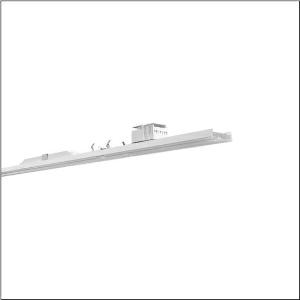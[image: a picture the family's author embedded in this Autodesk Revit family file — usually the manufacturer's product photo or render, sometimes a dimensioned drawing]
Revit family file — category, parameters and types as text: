
# Revit family: licross_r__21_recessed_mo_52tl14dnd7xf_36eb
name_source: partatom
category: Lighting Fixtures
units: mm (PartAtom-declared; Revit-internal decimal feet)

## family parameters
Cut with Voids When Loaded = No
Host = Face
Light Source = No
Part Type = Normal
Room Calculation Point = No
Round Connector Dimension = Use Diameter
Shared = No

## types (1)
- --- (1 x LED, 7330 lm, 61.1 W, 4000K)
    Apparent Load = 61 VA
    CIE Flux Codes = 56 84 97 100 100
    Color Rendering = 90
    Color Temperature = 4000K
    Default Elevation = 1800 mm
    Description = Licross® 21 Recessed MO, luminaire insert, of sheet steel, galvanised, coil coated, white, length: 1.500mm, width: 66mm, height: 67mm, LED rated luminous flux: 7.330lm, light colour: 940, control gear: DALI 2, control gear: ECG DALI, with plug, 5-pole, with phase selection, mains connection: 220..240V, AC, 50/60Hz, rated input power: 61W, halogen-free wiring, primary optical cover: cover, of PMMA, light emission: direct distribution, primary light characteristic: asymmetric, protection rating (complete): IP40, insulation class (complete): insulation class I (protective earthing), certification: CE, ENEC, VDE, UKCA, protection symbol: D if used in an environment without relevant dust loads with corresponding accessories, impact resistance: IK06, permissible ambient temperature for indoor applications: -25..+35°C, corresponds to IFS (International Featured Standards) requirements for safety and quality in the food industry, reducing of maximum allowable ambient temperature of 5°C with ceiling mounting, LABS conformity tested according to VDMA 24364:2018-05, packaging unit: 1 piece
    Height = 58 mm
    Lamp = 1 x LED
    Lamp Light Flux = 7330 lm
    Lamp Power = 61.1 W
    Lamp count = 1
    Length = 1500 mm
    Luminous efficacy = 120 lm/W
    Manufacturer = Siteco
    ModVariant = No
    Model = 52TL14DND7XF
    Mounting Place = Ceiling
    Mounting Type = Pendant
    Number of Poles = 1
    OnlyDefault = Yes
    Power Factor = 1
    Product Name = Licross® 21 Recessed MO
    Product group = luminaire insert
    ProductGroupID = 901
    Protection Class = Protection class I
    Protection Degree = IP 40
    RLX_Detail_Level = 1
    RLX_Emergency_Light_Flux = 0 lm
    RLX_Emergency_Type = 0
    RLX_Emergency_Type_DB = No
    RlxData = <blob elided: 23049 chars, md5=57ccac94>
    Socket = socket
    Standby Power = 0 W
    System Light Flux = 7330 lm
    System Power = 61 W
    Type Comments = factory setting: luminous flux: 100 % | dim-lin: 254 | 405 mA
    Type Image = l_1296935.jpg
    URL = http://relux.com
    VarID = @adj_136275
    Voltage = 0 V
    Weight = 0.00 kg
    Width = 66 mm

## geometry (parser evidence)
native form markers: Blend x4, Sweep x11
no freeform markers — native parametric forms only
